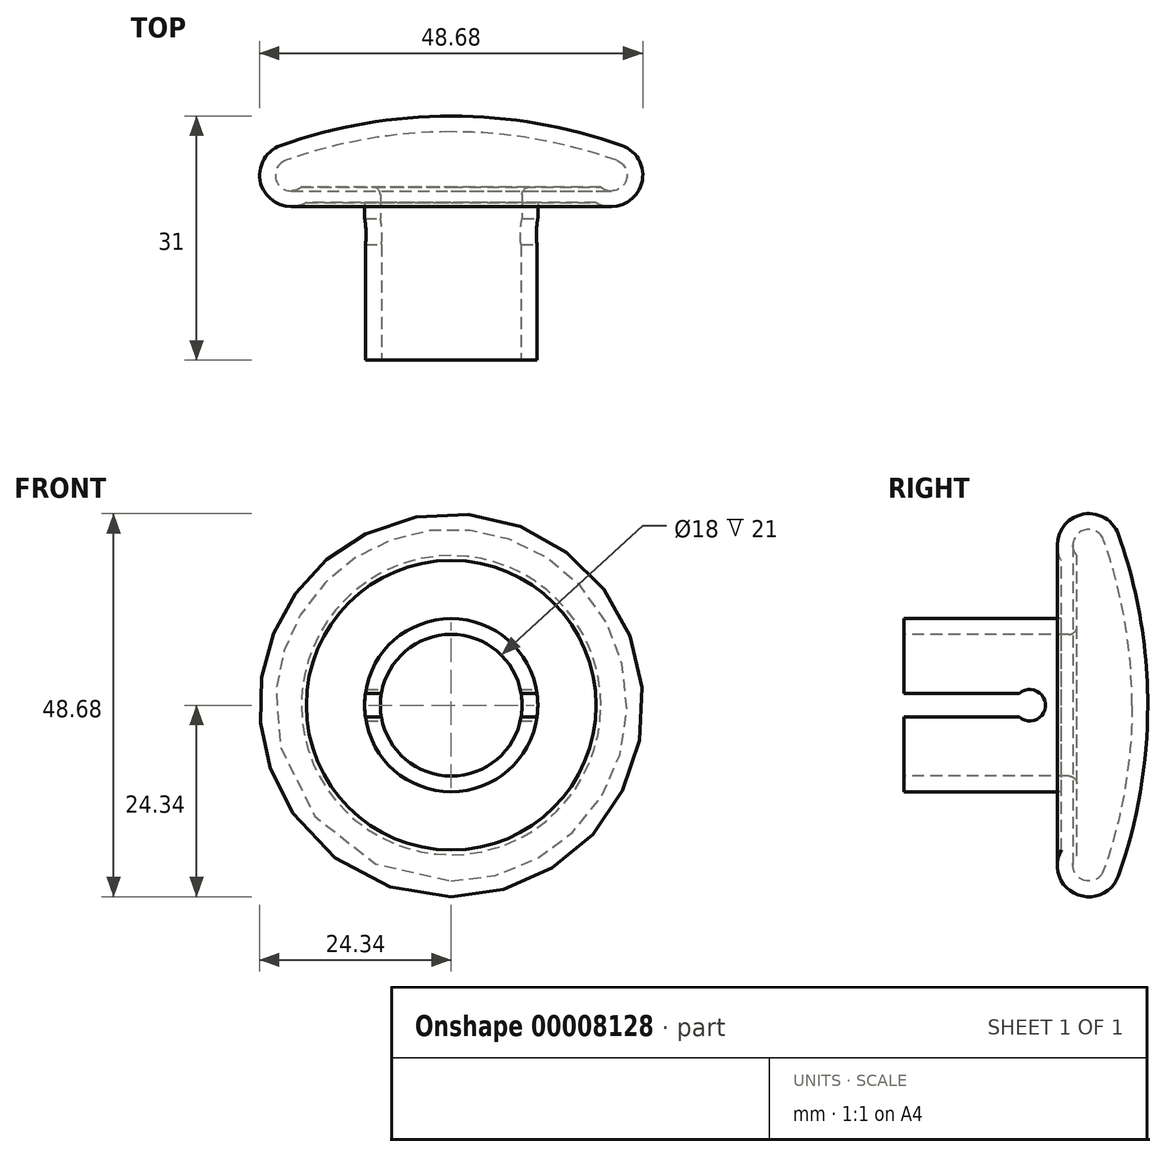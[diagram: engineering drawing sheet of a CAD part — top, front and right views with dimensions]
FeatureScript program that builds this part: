
annotation { "Feature Type Name" : "Feature", "Feature Type Description" : "" }
export const myFeature = defineFeature(function(context is Context, id is Id, definition is map)
    precondition{}
    {
        {
            var Q0;
            Q0=qCreatedBy(makeId("Right.planeOp"),FACE);
            var sketch = newSketch(context, id + "F0", { "sketchPlane" : qUnion([Q0])});
            skLineSegment(sketch, "E0", {"start": v(0, 0) * mm, "end": v(43.32, 0) * mm, "construction": true});
            skLineSegment(sketch, "E1", {"start": v(0, 11) * mm, "end": v(20, 11) * mm});
            skLineSegment(sketch, "E2", {"start": v(20, 11) * mm, "end": v(20, 18.4) * mm});
            skLineSegment(sketch, "E3", {"start": v(0, 11) * mm, "end": v(0, 9) * mm});
            skLineSegment(sketch, "E4", {"start": v(0, 9) * mm, "end": v(20, 9) * mm});
            skArc(sketch, "E5", {"start": v(27.27, 21.67) * mm, "mid": v(21.86, 23.98) * mm, "end": v(20, 18.4) * mm});
            skArc(sketch, "E6", {"start": v(31, 0) * mm, "mid": v(30.06, 11) * mm, "end": v(27.27, 21.67) * mm});
            skLineSegment(sketch, "E7", {"start": v(20, 0) * mm, "end": v(31, 0) * mm});
            skLineSegment(sketch, "E8.0", {"start": v(22, 10) * mm, "end": v(22, 19.01) * mm});
            skArc(sketch, "E8.1", {"start": v(25.38, 21) * mm, "mid": v(22.49, 22.06) * mm, "end": v(22, 19.01) * mm});
            skArc(sketch, "E8.2", {"start": v(29, 0) * mm, "mid": v(28.09, 10.66) * mm, "end": v(25.38, 21) * mm});
            skLineSegment(sketch, "E9", {"start": v(21, 9) * mm, "end": v(20, 9) * mm});
            skPoint(sketch, "E10.visualSharp", {"position": v(22, 9) * mm});
            skArc(sketch, "E10.filletArc", {"start": v(21, 9) * mm, "mid": v(21.7, 9.3) * mm, "end": v(22, 10) * mm});
            skSolve(sketch);
        }
        {
            var Q0;
            Q0 = qSketchRegion(id + "F0", true);
            var Q1;
            Q1=sQuery(id+"F0.wireOp",EDGE,"E0");
            revolve(context, id + "F1", {"entities" : qUnion([Q0]), "axis" : qUnion([Q1]), "revolveType" : RevolveType.FULL});
        }
        {
            var Q0;
            Q0=qCreatedBy(makeId("Right.planeOp"),FACE);
            var sketch = newSketch(context, id + "F2", { "sketchPlane" : qUnion([Q0])});
            skLineSegment(sketch, "E11", {"start": v(0, 1.5) * mm, "end": v(0, -1.5) * mm});
            skLineSegment(sketch, "E12", {"start": v(0, -1.5) * mm, "end": v(14.68, -1.5) * mm});
            skLineSegment(sketch, "E13", {"start": v(14.68, 1.5) * mm, "end": v(0, 1.5) * mm});
            skLineSegment(sketch, "E14", {"start": v(0, 0) * mm, "end": v(9.55, 0) * mm, "construction": true});
            skArc(sketch, "E15", {"start": v(14.68, -1.5) * mm, "mid": v(18, 0) * mm, "end": v(14.68, 1.5) * mm});
            skPoint(sketch, "E16.orphan", {"position": v(16, 1.5) * mm});
            skSolve(sketch);
        }
        {
            var Q0;
            Q0 = qSketchRegion(id + "F2", true);
            extrude(context, id + "F3", {"entities" : qUnion([Q0]), "operationType" : NewBodyOperationType.REMOVE, "endBound" : BoundingType.SYMMETRIC, "oppositeDirection" : true, "depth" : 25 * mm});
        }
    });
